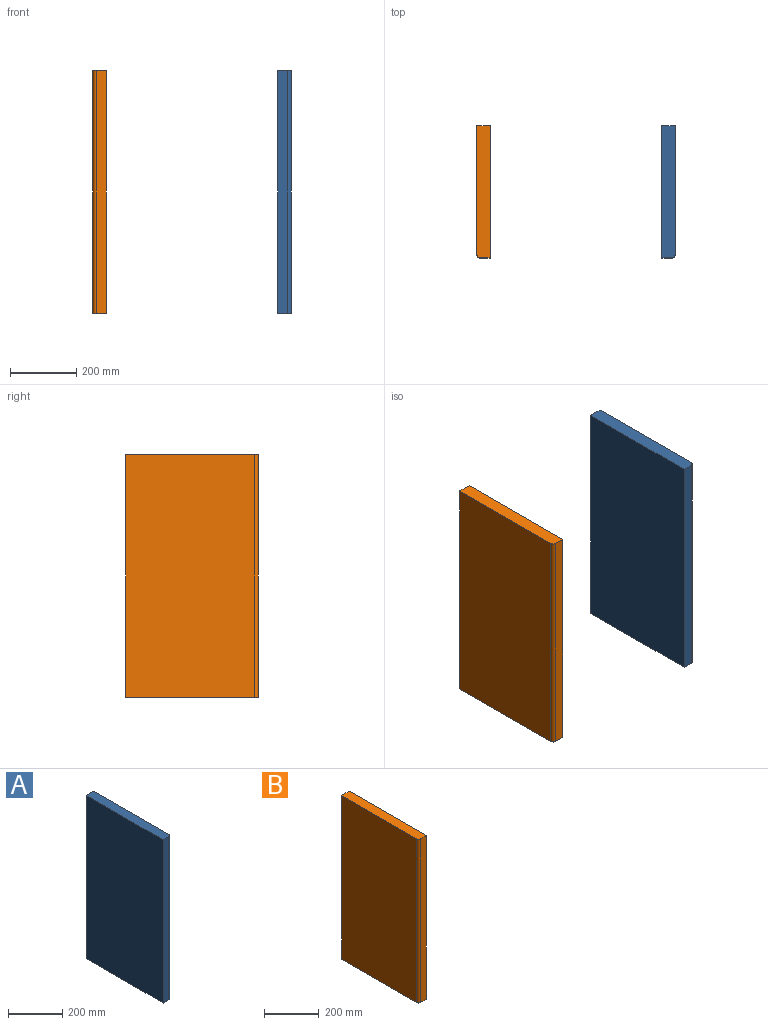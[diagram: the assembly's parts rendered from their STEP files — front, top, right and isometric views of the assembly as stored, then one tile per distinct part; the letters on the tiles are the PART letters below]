
ASSEMBLY  parts=2 mates=1
PART A: 7 faces, bbox 40x400x734 mm
  f0: plane 734x390mm, normal (1,0,0), area 286260mm2, adj f3,f4,f5,f6
  f1: plane 734x30mm, normal (0,-1,0), area 22020mm2, adj f2,f4,f5,f6
  f2: plane 734x400mm, normal (-1,0,0), area 293600mm2, adj f1,f3,f4,f5
  f3: plane 734x40mm, normal (0,1,0), area 29360mm2, adj f0,f2,f4,f5
  f4: plane 400x40mm, normal (0,0,1), area 15978.5mm2, adj f0,f1,f2,f3,f6
  f5: plane 400x40mm, normal (0,0,-1), area 15978.5mm2, adj f0,f1,f2,f3,f6
  f6: cylinder r=10mm len=734mm, axis (0,0,1), area 11529.6mm2, adj f0,f1,f4,f5
PART B: 7 faces, bbox 40x400x734 mm
  f0: plane 734x390mm, normal (-1,0,0), area 286260mm2, adj f3,f4,f5,f6
  f1: plane 734x30mm, normal (0,-1,0), area 22020mm2, adj f2,f4,f5,f6
  f2: plane 734x400mm, normal (1,0,0), area 293600mm2, adj f1,f3,f4,f5
  f3: plane 734x40mm, normal (0,1,0), area 29360mm2, adj f0,f2,f4,f5
  f4: plane 400x40mm, normal (0,0,1), area 15978.5mm2, adj f0,f1,f2,f3,f6
  f5: plane 400x40mm, normal (0,0,-1), area 15978.5mm2, adj f0,f1,f2,f3,f6
  f6: cylinder r=10mm len=734mm, axis (0,0,1), area 11529.6mm2, adj f0,f1,f4,f5
PLACE A t=(338.38,-157.03,-29.93)mm
PLACE B t=(-261.62,-157.03,-29.93)mm
MATE planar A.f4 <-> B.f4  axis (0,0,1) through (263.53,220.6,704.07)mm
